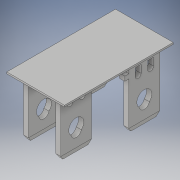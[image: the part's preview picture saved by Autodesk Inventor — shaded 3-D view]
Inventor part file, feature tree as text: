
AUTODESK INVENTOR PART (.ipt)
format: ipt  version: 2019 (Build 230136000, 136)  size: 235,520 bytes
history: native  units: in
note: dims shown in document units (in); Inventor stores cm internally (conversion verified against a paired STEP export)
features: extrude x10, sketch x10, other x7
ambient origin geometry x8: Origin, YZ Plane, XZ Plane, XY Plane, X Axis, Y Axis, Z Axis, Center Point
bodies: Solid1 (feature_tree)
feature tree (27):
  extrude  "Extrusion1"  Depth=0.031in TaperAngle=0.0deg
  extrude  "Extrusion2"  Depth=0.031in TaperAngle=0.0deg
  extrude  "Extrusion3"  Depth=0.031in TaperAngle=0.0deg
  extrude  "Extrusion4"  Depth=0.7in TaperAngle=0.0deg
  extrude  "Extrusion5"  Depth=0.7in TaperAngle=0.0deg
  extrude  "Extrusion6"  [1 undecoded]
  extrude  "Extrusion7"  [1 undecoded]
  extrude  "Extrusion8"  [1 undecoded]
  extrude  "Extrusion9"  [1 undecoded]
  extrude  "Extrusion10"  [1 undecoded]
  other  "to_body_XY"
  other  "to_body_YZ"
  other  "to_body_ZX"
  other  "to_body_X"
  other  "to_body_Y"
  other  "to_body_Z"
  other  "to_body_Center"
  sketch  "Sketch_1"  dims[d0=0.01in d1=0.0in d2=0.031in d3=0.0in]
  sketch  "Sketch_2"  dims[d4=0.031in d5=0.0in d6=0.031in d7=0.0in]
  sketch  "Sketch_3"  dims[d8=0.031in d9=0.0in d10=0.7in d11=0.0in]
  sketch  "Sketch_4"  dims[d12=0.7in d13=0.0in d14=0.7in d15=0.0in]
  sketch  "Sketch_5"  dims[d16=0.7in d17=0.0in d18=0.7in d19=0.0in]
  sketch  "Sketch_6"
  sketch  "Sketch_8"
  sketch  "Sketch_9"
  sketch  "Sketch_10"
  sketch  "Sketch_11"
note: 5 required parameter values undecoded (feature->parameter linkage not recoverable at this tier; creation-order binding heuristic only, values carry confidence <= 0.55)
